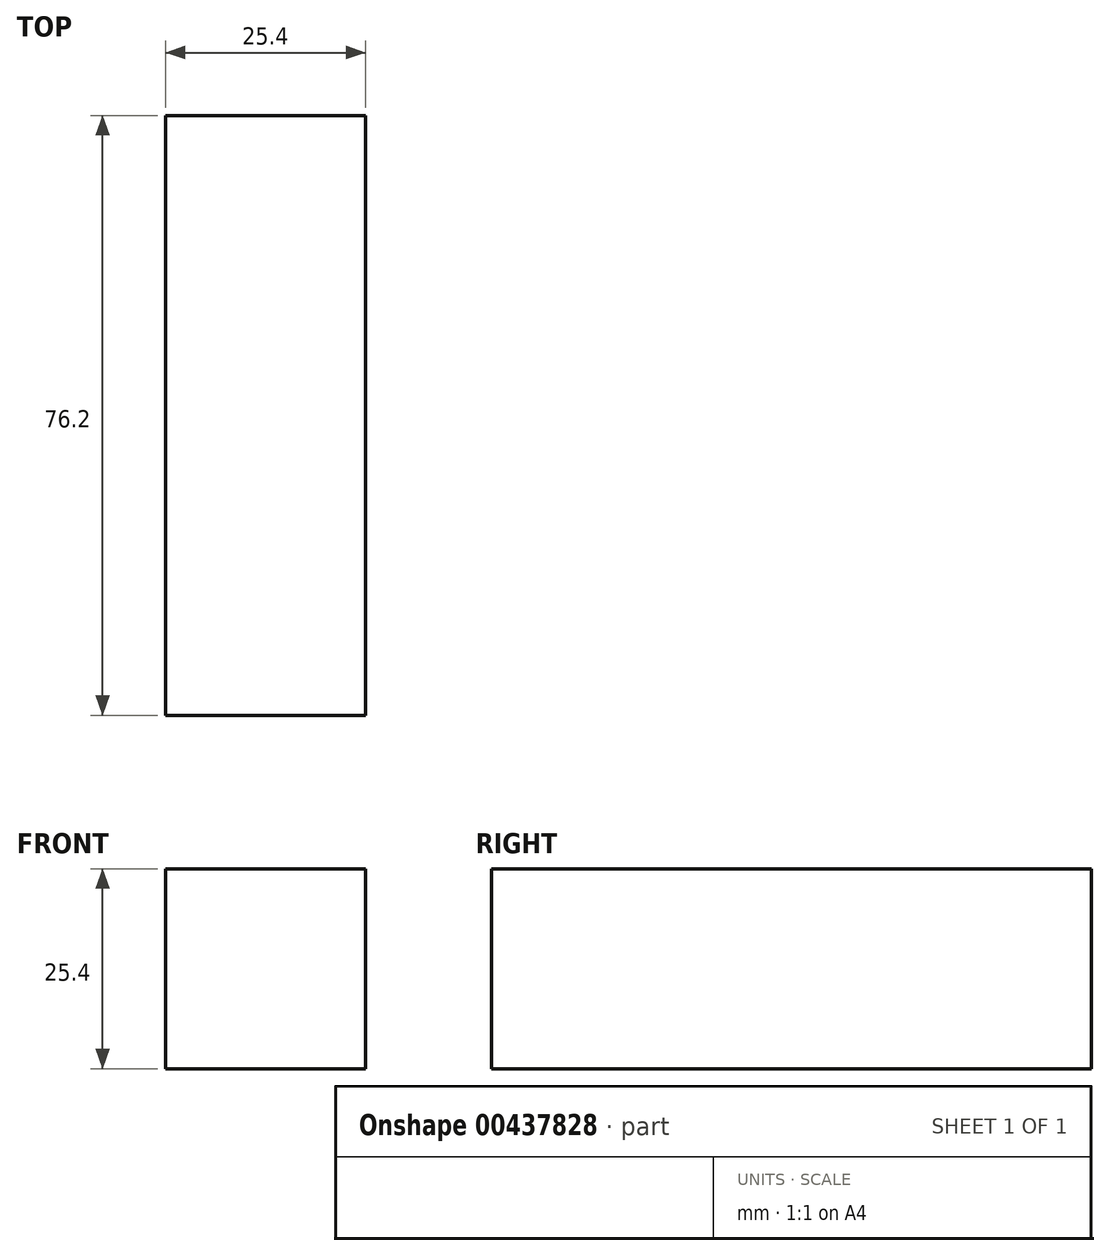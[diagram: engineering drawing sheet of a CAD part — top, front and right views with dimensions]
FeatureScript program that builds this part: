
annotation { "Feature Type Name" : "Feature", "Feature Type Description" : "" }
export const myFeature = defineFeature(function(context is Context, id is Id, definition is map)
    precondition{}
    {
        {
            var Q0;
            Q0=qCreatedBy(makeId("Front.planeOp"),FACE);
            var sketch = newSketch(context, id + "F0", { "sketchPlane" : qUnion([Q0])});
            skLineSegment(sketch, "E0.bottom", {"start": v(12.7, 12.7) * mm, "end": v(-12.7, 12.7) * mm});
            skLineSegment(sketch, "E0.top", {"start": v(12.7, -12.7) * mm, "end": v(-12.7, -12.7) * mm});
            skLineSegment(sketch, "E0.left", {"start": v(12.7, 12.7) * mm, "end": v(12.7, -12.7) * mm});
            skLineSegment(sketch, "E0.right", {"start": v(-12.7, 12.7) * mm, "end": v(-12.7, -12.7) * mm});
            skPoint(sketch, "E0.middle", {"position": v(0, 0) * mm});
            skSolve(sketch);
        }
        {
            var Q0;
            Q0=makeQuery(id+"F0.imprint","IMPRINT",FACE,{"disambiguationData":[TD([[makeQuery(id+"F0.imprint","IMPRINT",EDGE,{"derivedFrom":sQuery(id+"F0.wireOp",EDGE,"E0.bottom")}),1.0]])]});
            extrude(context, id + "F1", {"entities" : qUnion([Q0]), "depth" : 76.2 * mm});
        }
    });
